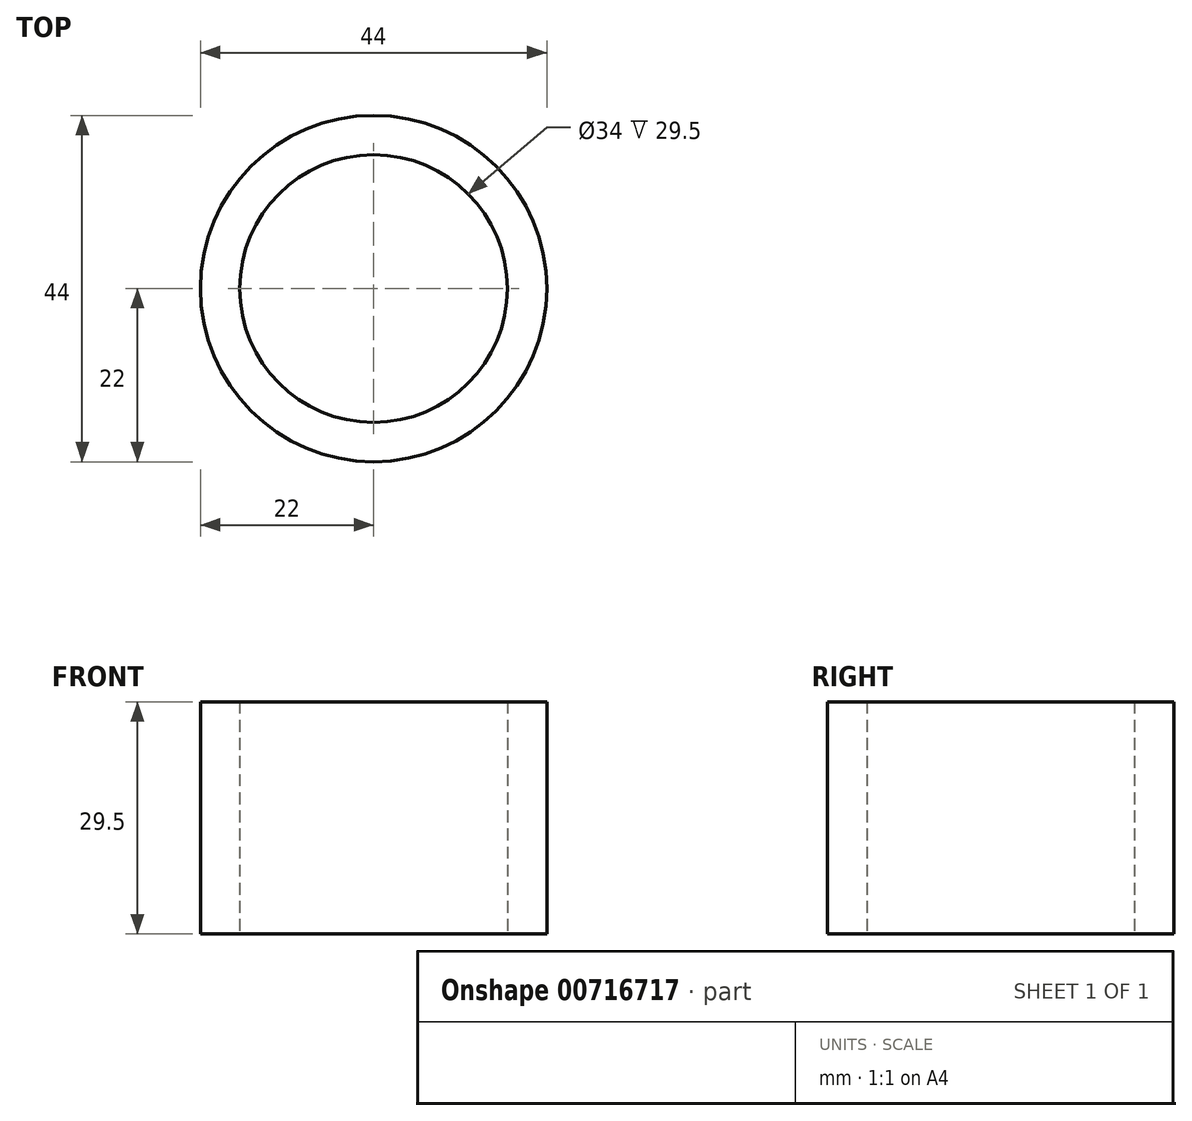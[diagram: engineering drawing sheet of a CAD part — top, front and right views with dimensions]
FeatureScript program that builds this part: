
annotation { "Feature Type Name" : "Feature", "Feature Type Description" : "" }
export const myFeature = defineFeature(function(context is Context, id is Id, definition is map)
    precondition{}
    {
        {
            var Q0;
            Q0=qCreatedBy(makeId("Top.planeOp"),FACE);
            var sketch = newSketch(context, id + "F0", { "sketchPlane" : qUnion([Q0])});
            skCircle(sketch, "E0", {"center": v(0, 0) * mm, "radius": 22 * mm});
            skCircle(sketch, "E1", {"center": v(0, 0) * mm, "radius": 17 * mm});
            skSolve(sketch);
        }
        {
            var Q0;
            Q0=makeQuery(id+"F0.imprint","IMPRINT",FACE,{"disambiguationData":[TD([[makeQuery(id+"F0.imprint","IMPRINT",EDGE,{"derivedFrom":sQuery(id+"F0.wireOp",EDGE,"E0")}),1.0]])]});
            extrude(context, id + "F1", {"entities" : qUnion([Q0]), "depth" : 29.5 * mm, "offsetDistance" : 25 * mm});
        }
    });
